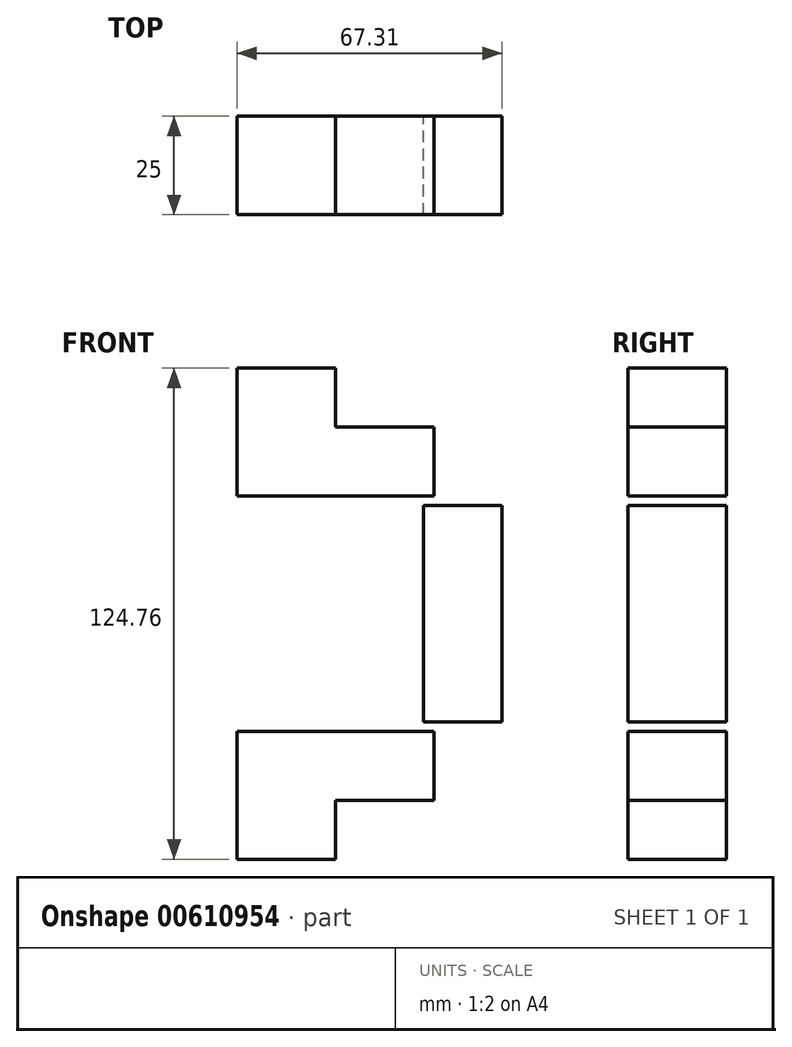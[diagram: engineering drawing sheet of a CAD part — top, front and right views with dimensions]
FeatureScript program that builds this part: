
annotation { "Feature Type Name" : "Feature", "Feature Type Description" : "" }
export const myFeature = defineFeature(function(context is Context, id is Id, definition is map)
    precondition{}
    {
        {
            var Q0;
            Q0=qCreatedBy(makeId("Front.planeOp"),FACE);
            var sketch = newSketch(context, id + "F0", { "sketchPlane" : qUnion([Q0])});
            skLineSegment(sketch, "E0.bottom", {"start": v(67.3, 27.5) * mm, "end": v(47.3, 27.5) * mm});
            skLineSegment(sketch, "E0.top", {"start": v(67.3, -27.5) * mm, "end": v(47.3, -27.5) * mm});
            skLineSegment(sketch, "E0.left", {"start": v(67.3, 27.5) * mm, "end": v(67.3, -27.5) * mm});
            skLineSegment(sketch, "E0.right", {"start": v(47.3, 27.5) * mm, "end": v(47.3, -27.5) * mm});
            skPoint(sketch, "E0.middle", {"position": v(57.3, 0) * mm});
            skLineSegment(sketch, "E1.bottom", {"start": v(0, 62.38) * mm, "end": v(25, 62.38) * mm});
            skLineSegment(sketch, "E1.top", {"start": v(0, 47.38) * mm, "end": v(25, 47.38) * mm});
            skLineSegment(sketch, "E1.left", {"start": v(0, 62.38) * mm, "end": v(0, 47.38) * mm});
            skLineSegment(sketch, "E1.right", {"start": v(25, 62.38) * mm, "end": v(25, 47.38) * mm});
            skLineSegment(sketch, "E2.bottom", {"start": v(0, 47.38) * mm, "end": v(50, 47.38) * mm});
            skLineSegment(sketch, "E2.top", {"start": v(0, 29.88) * mm, "end": v(50, 29.88) * mm});
            skLineSegment(sketch, "E2.left", {"start": v(0, 47.38) * mm, "end": v(0, 29.88) * mm});
            skLineSegment(sketch, "E2.right", {"start": v(50, 47.38) * mm, "end": v(50, 29.88) * mm});
            skLineSegment(sketch, "E3", {"start": v(118.04, 0) * mm, "end": v(227.18, 0) * mm, "construction": true});
            skLineSegment(sketch, "E4.MirrorCS", {"start": v(0, -47.38) * mm, "end": v(25, -47.38) * mm});
            skLineSegment(sketch, "E5.MirrorCS", {"start": v(0, -47.38) * mm, "end": v(0, -29.88) * mm});
            skLineSegment(sketch, "E6.MirrorCS", {"start": v(0, -62.38) * mm, "end": v(0, -47.38) * mm});
            skLineSegment(sketch, "E7.MirrorCS", {"start": v(25, -62.38) * mm, "end": v(25, -47.38) * mm});
            skLineSegment(sketch, "E8.MirrorCS", {"start": v(0, -47.38) * mm, "end": v(50, -47.38) * mm});
            skLineSegment(sketch, "E9.MirrorCS", {"start": v(0, -29.88) * mm, "end": v(50, -29.88) * mm});
            skLineSegment(sketch, "E10.MirrorCS", {"start": v(50, -47.38) * mm, "end": v(50, -29.88) * mm});
            skLineSegment(sketch, "E11.MirrorCS", {"start": v(0, -62.38) * mm, "end": v(25, -62.38) * mm});
            skSolve(sketch);
        }
        {
            var Q0;
            Q0=makeQuery(id+"F0.imprint","IMPRINT",FACE,{"disambiguationData":[TD([[makeQuery(id+"F0.imprint","IMPRINT",EDGE,{"derivedFrom":sQuery(id+"F0.wireOp",EDGE,"E2.top")}),1.0]])]});
            var Q1;
            Q1=makeQuery(id+"F0.imprint","IMPRINT",FACE,{"disambiguationData":[TD([[makeQuery(id+"F0.imprint","IMPRINT",EDGE,{"derivedFrom":sQuery(id+"F0.wireOp",EDGE,"E1.bottom")}),-1.0]])]});
            var Q2;
            {var subQ3=sQuery(id+"F0.wireOp",EDGE,"E5.MirrorCS");Q2=makeQuery(id+"F0.imprint","IMPRINT",FACE,{"disambiguationData":[TD([[makeQuery(id+"F0.imprint","IMPRINT",EDGE,{"derivedFrom":subQ3}),-1.0]])]});}
            var Q3;
            {var subQ0=sQuery(id+"F0.wireOp",EDGE,"E6.MirrorCS");Q3=makeQuery(id+"F0.imprint","IMPRINT",FACE,{"disambiguationData":[TD([[makeQuery(id+"F0.imprint","IMPRINT",EDGE,{"derivedFrom":subQ0}),-1.0]])]});}
            var Q4;
            Q4=makeQuery(id+"F0.imprint","IMPRINT",FACE,{"disambiguationData":[TD([[makeQuery(id+"F0.imprint","IMPRINT",EDGE,{"derivedFrom":sQuery(id+"F0.wireOp",EDGE,"E0.bottom")}),1.0]])]});
            extrude(context, id + "F1", {"entities" : qUnion([Q0, Q1, Q2, Q3, Q4]), "depth" : 25 * mm, "offsetDistance" : 25 * mm, "symmetric" : true});
        }
    });
